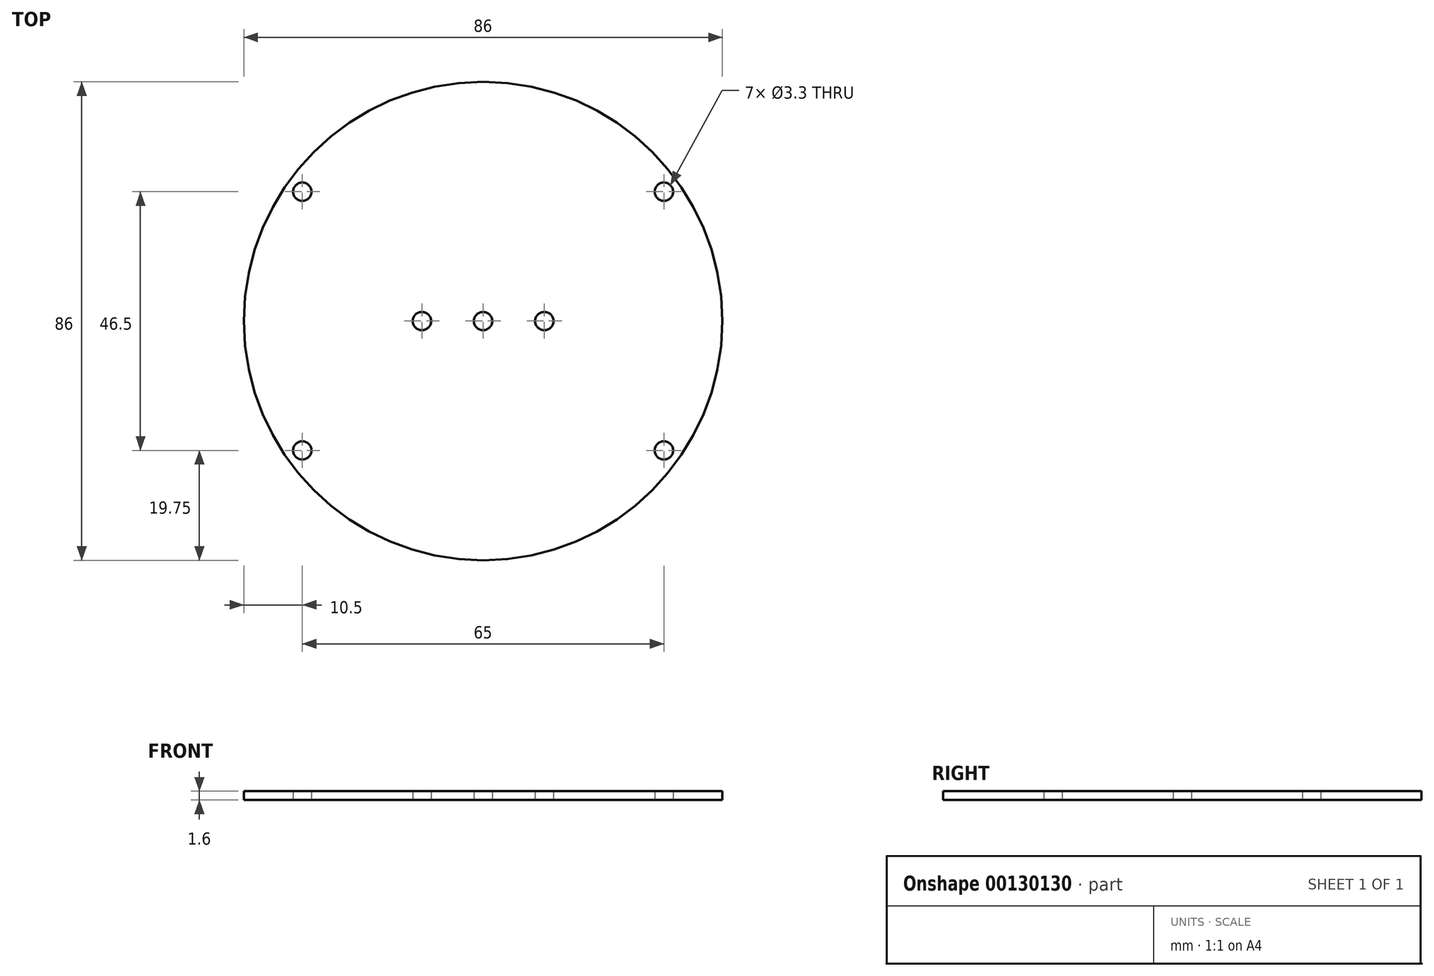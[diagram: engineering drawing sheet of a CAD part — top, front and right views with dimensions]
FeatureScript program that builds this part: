
annotation { "Feature Type Name" : "Feature", "Feature Type Description" : "" }
export const myFeature = defineFeature(function(context is Context, id is Id, definition is map)
    precondition{}
    {
        {
            var Q0;
            Q0=qCreatedBy(makeId("Top.planeOp"),FACE);
            var sketch = newSketch(context, id + "F0", { "sketchPlane" : qUnion([Q0])});
            skCircle(sketch, "E0", {"center": v(0, 0) * mm, "radius": 43 * mm});
            skCircle(sketch, "E1", {"center": v(-32.5, 23.25) * mm, "radius": 1.65 * mm});
            skCircle(sketch, "E2", {"center": v(32.5, 23.25) * mm, "radius": 1.65 * mm});
            skCircle(sketch, "E3", {"center": v(-32.5, -23.25) * mm, "radius": 1.65 * mm});
            skCircle(sketch, "E4", {"center": v(32.5, -23.25) * mm, "radius": 1.65 * mm});
            skCircle(sketch, "E5", {"center": v(0, 0) * mm, "radius": 25 * mm});
            skCircle(sketch, "E6", {"center": v(0, 0) * mm, "radius": 1.65 * mm});
            skCircle(sketch, "E7", {"center": v(-11, 0) * mm, "radius": 1.65 * mm});
            skCircle(sketch, "E8", {"center": v(11, 0) * mm, "radius": 1.65 * mm});
            skSolve(sketch);
        }
        {
            var Q0;
            Q0=makeQuery(id+"F0.imprint","IMPRINT",FACE,{"disambiguationData":[TD([[makeQuery(id+"F0.imprint","IMPRINT",EDGE,{"derivedFrom":sQuery(id+"F0.wireOp",EDGE,"E0")}),1.0]])]});
            var Q1;
            Q1=makeQuery(id+"F0.imprint","IMPRINT",FACE,{"disambiguationData":[TD([[makeQuery(id+"F0.imprint","IMPRINT",EDGE,{"derivedFrom":sQuery(id+"F0.wireOp",EDGE,"E5")}),1.0]])]});
            extrude(context, id + "F1", {"entities" : qUnion([Q0, Q1]), "depth" : 1.6 * mm});
        }
    });
